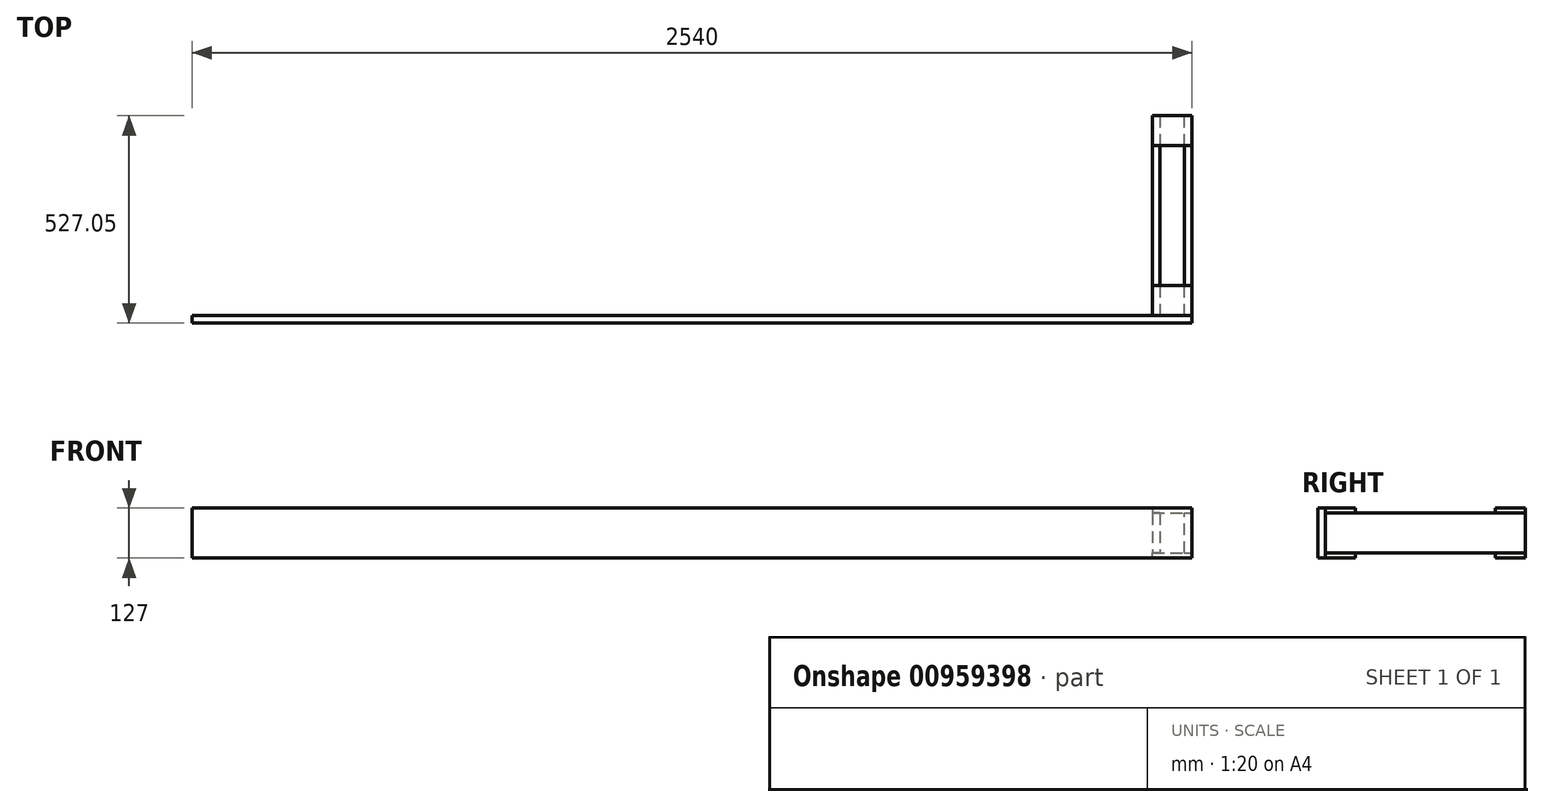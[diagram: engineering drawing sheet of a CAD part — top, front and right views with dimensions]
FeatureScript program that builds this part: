
annotation { "Feature Type Name" : "Feature", "Feature Type Description" : "" }
export const myFeature = defineFeature(function(context is Context, id is Id, definition is map)
    precondition{}
    {
        {
            assignVariable(context, id + "F0", {"name" : "Width", "anyValue" : 100});
        }
        {
            var Q0;
            Q0=qCreatedBy(makeId("Right.planeOp"),FACE);
            var sketch = newSketch(context, id + "F1", { "sketchPlane" : qUnion([Q0])});
            skLineSegment(sketch, "E0.bottom", {"start": v(0, 12.7) * mm, "end": v(508, 12.7) * mm});
            skLineSegment(sketch, "E0.top", {"start": v(0, 114.3) * mm, "end": v(508, 114.3) * mm});
            skLineSegment(sketch, "E0.left", {"start": v(0, 12.7) * mm, "end": v(0, 114.3) * mm});
            skLineSegment(sketch, "E0.right", {"start": v(508, 12.7) * mm, "end": v(508, 114.3) * mm});
            skSolve(sketch);
        }
        {
            var Q0;
            Q0=makeQuery(id+"F1.imprint","IMPRINT",FACE,{"disambiguationData":[TD([[makeQuery(id+"F1.imprint","IMPRINT",EDGE,{"derivedFrom":sQuery(id+"F1.wireOp",EDGE,"E0.bottom")}),1.0]])]});
            extrude(context, id + "F2", {"entities" : qUnion([Q0]), "oppositeDirection" : true, "depth" : 19.05 * mm, "offsetDistance" : 25.4 * mm});
        }
        {
            var Q0;
            Q0=qCreatedBy(makeId("Right.planeOp"),FACE);
            var sketch = newSketch(context, id + "F3", { "sketchPlane" : qUnion([Q0])});
            skPoint(sketch, "E1.0", {"position": v(0, 114.3) * mm});
            skLineSegment(sketch, "E2.bottom", {"start": v(0, 114.3) * mm, "end": v(76.2, 114.3) * mm});
            skLineSegment(sketch, "E2.top", {"start": v(0, 127) * mm, "end": v(76.2, 127) * mm});
            skLineSegment(sketch, "E2.left", {"start": v(0, 114.3) * mm, "end": v(0, 127) * mm});
            skLineSegment(sketch, "E2.right", {"start": v(76.2, 114.3) * mm, "end": v(76.2, 127) * mm});
            skPoint(sketch, "E3.0", {"position": v(508, 114.3) * mm});
            skPoint(sketch, "E4.0", {"position": v(508, 12.7) * mm});
            skPoint(sketch, "E5.0", {"position": v(0, 12.7) * mm});
            skLineSegment(sketch, "E6.bottom", {"start": v(0, 12.7) * mm, "end": v(76.2, 12.7) * mm});
            skLineSegment(sketch, "E6.top", {"start": v(0, 0) * mm, "end": v(76.2, 0) * mm});
            skLineSegment(sketch, "E6.left", {"start": v(0, 12.7) * mm, "end": v(0, 0) * mm});
            skLineSegment(sketch, "E6.right", {"start": v(76.2, 12.7) * mm, "end": v(76.2, 0) * mm});
            skLineSegment(sketch, "E7.bottom", {"start": v(508, 12.7) * mm, "end": v(431.8, 12.7) * mm});
            skLineSegment(sketch, "E7.top", {"start": v(508, 0) * mm, "end": v(431.8, 0) * mm});
            skLineSegment(sketch, "E7.left", {"start": v(508, 12.7) * mm, "end": v(508, 0) * mm});
            skLineSegment(sketch, "E7.right", {"start": v(431.8, 12.7) * mm, "end": v(431.8, 0) * mm});
            skLineSegment(sketch, "E8.bottom", {"start": v(508, 114.3) * mm, "end": v(431.8, 114.3) * mm});
            skLineSegment(sketch, "E8.top", {"start": v(508, 127) * mm, "end": v(431.8, 127) * mm});
            skLineSegment(sketch, "E8.left", {"start": v(508, 114.3) * mm, "end": v(508, 127) * mm});
            skLineSegment(sketch, "E8.right", {"start": v(431.8, 114.3) * mm, "end": v(431.8, 127) * mm});
            skSolve(sketch);
        }
        {
            var Q0;
            Q0=qCreatedBy(makeId("Right.planeOp"),FACE);
            cPlane(context, id + "F4", {"entities" : qUnion([Q0]), "cplaneType" : CPlaneType.OFFSET, "offset" : (getVariable(context, 'Width')) * mm, "oppositeDirection" : true, "width" : 152.4 * mm, "height" : 152.4 * mm});
        }
        {
            var Q0;
            Q0=qSketchRegion(id+"F3",true);
            var Q1;
            Q1=qCreatedBy(id+"F4.planeOp",FACE);
            extrude(context, id + "F5", {"entities" : qUnion([Q0]), "endBound" : BoundingType.UP_TO_SURFACE, "oppositeDirection" : true, "depth" : 25.4 * mm, "endBoundEntityFace" : qUnion([Q1]), "offsetDistance" : 25.4 * mm});
        }
        {
            var Q0;
            Q0=makeQuery(id+"F2.opExtrude","SWEPT_BODY",BODY,{"disambiguationData":[OSD([sQuery(id+"F1.wireOp",EDGE,"E0.bottom"),sQuery(id+"F1.wireOp",EDGE,"E0.top"),sQuery(id+"F1.wireOp",EDGE,"E0.left"),sQuery(id+"F1.wireOp",EDGE,"E0.right")])]});
            transform(context, id + "F6", {"entities" : qUnion([Q0]), "transformType" : TransformType.TRANSLATION_3D, "dx" : -891.54 * mm, "dy" : 0 * mm, "dz" : 0 * mm, "makeCopy" : true});
        }
        {
            var Q0;
            Q0=makeQuery(id+"F6.opPattern","COPY",BODY,{"derivedFrom":makeQuery(id+"F2.opExtrude","SWEPT_BODY",BODY,{"disambiguationData":[OSD([sQuery(id+"F1.wireOp",EDGE,"E0.bottom"),sQuery(id+"F1.wireOp",EDGE,"E0.top"),sQuery(id+"F1.wireOp",EDGE,"E0.left"),sQuery(id+"F1.wireOp",EDGE,"E0.right")])]}),"instanceName":"1"});
            deleteBodies(context, id + "F7", {"entities" : qUnion([Q0])});
        }
        {
            var Q0;
            Q0=qCreatedBy(id+"F4.planeOp",FACE);
            var sketch = newSketch(context, id + "F8", { "sketchPlane" : qUnion([Q0])});
            skPoint(sketch, "E9.0", {"position": v(508, 114.3) * mm});
            skPoint(sketch, "E10.0", {"position": v(508, 12.7) * mm});
            skPoint(sketch, "E11.0", {"position": v(0, 12.7) * mm});
            skPoint(sketch, "E12.0", {"position": v(0, 114.3) * mm});
            skLineSegment(sketch, "E13.bottom", {"start": v(508, 114.3) * mm, "end": v(0, 114.3) * mm});
            skLineSegment(sketch, "E13.top", {"start": v(508, 12.7) * mm, "end": v(0, 12.7) * mm});
            skLineSegment(sketch, "E13.left", {"start": v(508, 114.3) * mm, "end": v(508, 12.7) * mm});
            skLineSegment(sketch, "E13.right", {"start": v(0, 114.3) * mm, "end": v(0, 12.7) * mm});
            skSolve(sketch);
        }
        {
            var Q0;
            Q0=qSketchRegion(id+"F8",true);
            extrude(context, id + "F9", {"entities" : qUnion([Q0]), "depth" : 19.05 * mm, "offsetDistance" : 25.4 * mm});
        }
        {
            var Q0;
            Q0=makeQuery(id+"F9.opExtrude","SWEPT_FACE",FACE,{"disambiguationData":[OSD([sQuery(id+"F8.wireOp",EDGE,"E13.right")])]});
            var sketch = newSketch(context, id + "F10", { "sketchPlane" : qUnion([Q0])});
            skPoint(sketch, "E14.0", {"position": v(-2540, 127) * mm});
            skLineSegment(sketch, "E15.0", {"start": v(-2540, 0) * mm, "end": v(0, 0) * mm});
            skLineSegment(sketch, "E16.bottom", {"start": v(0, 0) * mm, "end": v(-2540, 0) * mm});
            skLineSegment(sketch, "E16.top", {"start": v(0, 127) * mm, "end": v(-2540, 127) * mm});
            skLineSegment(sketch, "E16.left", {"start": v(0, 0) * mm, "end": v(0, 127) * mm});
            skLineSegment(sketch, "E16.right", {"start": v(-2540, 0) * mm, "end": v(-2540, 127) * mm});
            skSolve(sketch);
        }
        {
            var Q0;
            Q0=qSketchRegion(id+"F10",true);
            extrude(context, id + "F11", {"entities" : qUnion([Q0]), "depth" : 19.05 * mm, "offsetDistance" : 25.4 * mm});
        }
    });
